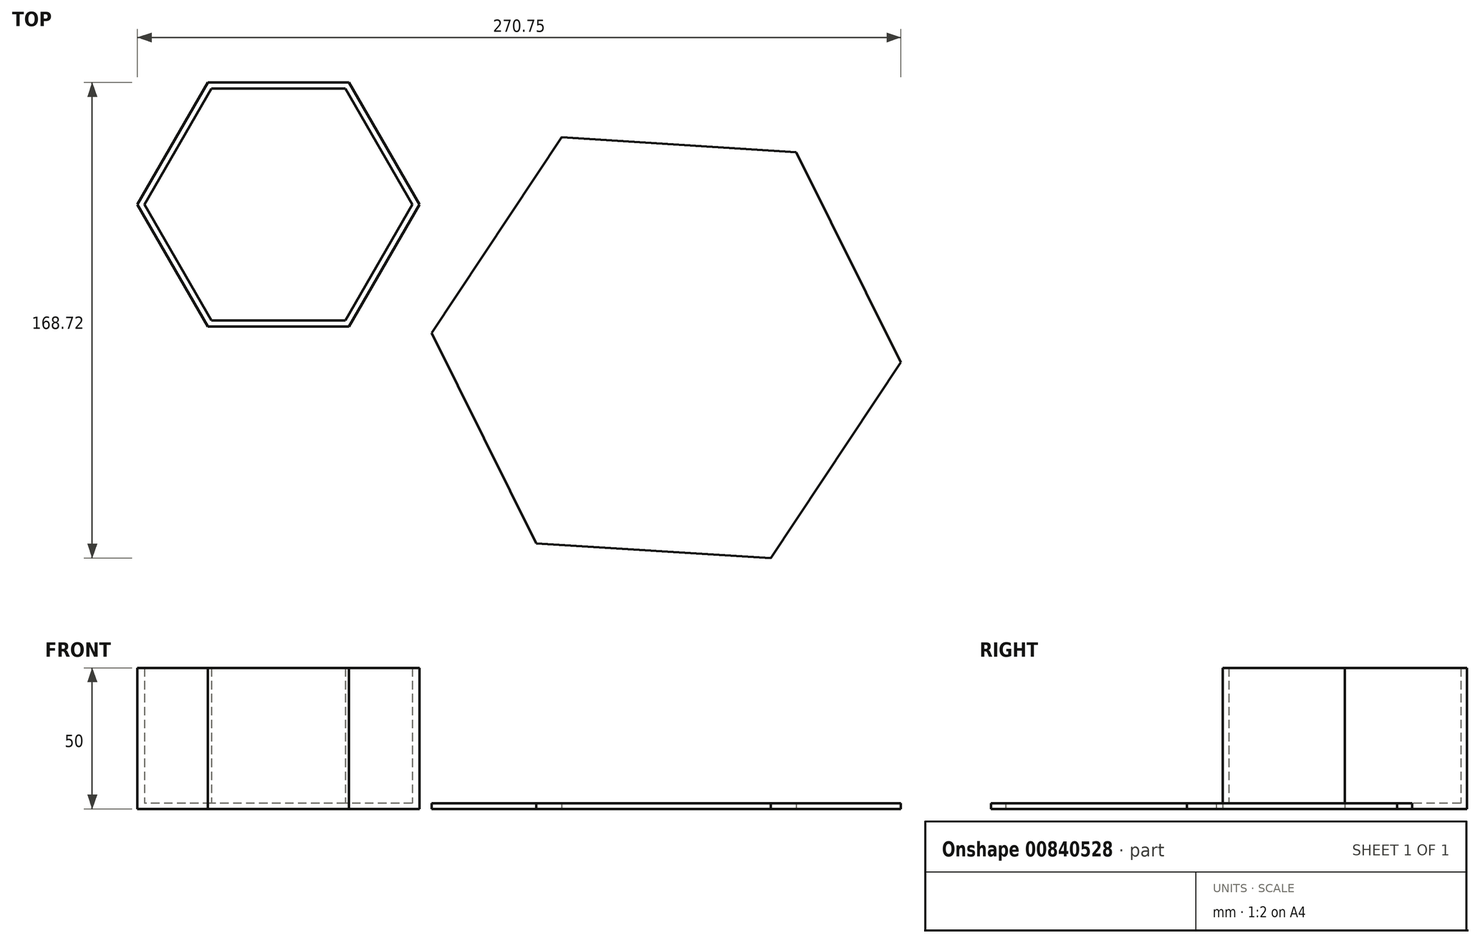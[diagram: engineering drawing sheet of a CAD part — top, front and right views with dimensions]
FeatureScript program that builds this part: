
annotation { "Feature Type Name" : "Feature", "Feature Type Description" : "" }
export const myFeature = defineFeature(function(context is Context, id is Id, definition is map)
    precondition{}
    {
        {
            var Q0;
            Q0=qCreatedBy(makeId("Top.planeOp"),FACE);
            var sketch = newSketch(context, id + "F0", { "sketchPlane" : qUnion([Q0])});
            skCircle(sketch, "E0.cCircle", {"center": v(0, 0) * mm, "radius": 43.3 * mm, "construction": true});
            skLineSegment(sketch, "E0.0", {"start": v(50, 0) * mm, "end": v(25, -43.3) * mm});
            skLineSegment(sketch, "E0.1", {"start": v(25, -43.3) * mm, "end": v(-25, -43.3) * mm});
            skLineSegment(sketch, "E0.2", {"start": v(-25, -43.3) * mm, "end": v(-50, 0) * mm});
            skLineSegment(sketch, "E0.3", {"start": v(-50, 0) * mm, "end": v(-25, 43.3) * mm});
            skLineSegment(sketch, "E0.4", {"start": v(-25, 43.3) * mm, "end": v(25, 43.3) * mm});
            skLineSegment(sketch, "E0.5", {"start": v(25, 43.3) * mm, "end": v(50, 0) * mm});
            skPoint(sketch, "E0.0.midPoint", {"position": v(37.5, -21.65) * mm});
            skCircle(sketch, "E1.cCircle", {"center": v(0, 0) * mm, "radius": 41.14 * mm, "construction": true});
            skLineSegment(sketch, "E1.0", {"start": v(-23.75, 41.14) * mm, "end": v(23.75, 41.14) * mm});
            skLineSegment(sketch, "E1.1", {"start": v(23.75, 41.14) * mm, "end": v(47.5, 0) * mm});
            skLineSegment(sketch, "E1.2", {"start": v(47.5, 0) * mm, "end": v(23.75, -41.14) * mm});
            skLineSegment(sketch, "E1.3", {"start": v(23.75, -41.14) * mm, "end": v(-23.75, -41.14) * mm});
            skLineSegment(sketch, "E1.4", {"start": v(-23.75, -41.14) * mm, "end": v(-47.5, 0) * mm});
            skLineSegment(sketch, "E1.5", {"start": v(-47.5, 0) * mm, "end": v(-23.75, 41.14) * mm});
            skPoint(sketch, "E1.0.midPoint", {"position": v(0, 41.14) * mm});
            skSolve(sketch);
        }
        {
            var Q0;
            Q0 = qSketchRegion(id + "F0", true);
            var Q1;
            Q1=makeQuery(id+"F0.imprint","IMPRINT",FACE,{"disambiguationData":[TD([[makeQuery(id+"F0.imprint","IMPRINT",EDGE,{"derivedFrom":sQuery(id+"F0.wireOp",EDGE,"E1.0")}),-1.0]])]});
            extrude(context, id + "F1", {"entities" : qUnion([Q0, Q1]), "depth" : 2 * mm, "offsetDistance" : 25 * mm});
        }
        {
            var Q0;
            Q0=makeQuery(id+"F0.imprint","IMPRINT",FACE,{"disambiguationData":[TD([[makeQuery(id+"F0.imprint","IMPRINT",EDGE,{"derivedFrom":sQuery(id+"F0.wireOp",EDGE,"E0.0")}),-1.0]])]});
            extrude(context, id + "F2", {"entities" : qUnion([Q0]), "operationType" : NewBodyOperationType.ADD, "depth" : 50 * mm, "offsetDistance" : 25 * mm});
        }
        {
            var Q0;
            Q0=qCreatedBy(makeId("Top.planeOp"),FACE);
            var sketch = newSketch(context, id + "F3", { "sketchPlane" : qUnion([Q0])});
            skCircle(sketch, "E2.cCircle", {"center": v(137.58, -50.78) * mm, "radius": 72.17 * mm, "construction": true});
            skLineSegment(sketch, "E2.0", {"start": v(220.75, -56) * mm, "end": v(174.64, -125.42) * mm});
            skLineSegment(sketch, "E2.1", {"start": v(174.64, -125.42) * mm, "end": v(91.47, -120.2) * mm});
            skLineSegment(sketch, "E2.2", {"start": v(91.47, -120.2) * mm, "end": v(54.4, -45.56) * mm});
            skLineSegment(sketch, "E2.3", {"start": v(54.4, -45.56) * mm, "end": v(100.5, 23.86) * mm});
            skLineSegment(sketch, "E2.4", {"start": v(100.5, 23.86) * mm, "end": v(183.68, 18.64) * mm});
            skLineSegment(sketch, "E2.5", {"start": v(183.68, 18.64) * mm, "end": v(220.75, -56) * mm});
            skPoint(sketch, "E2.0.midPoint", {"position": v(197.7, -90.7) * mm});
            skSolve(sketch);
        }
        {
            var Q0;
            Q0=makeQuery(id+"F3.imprint","IMPRINT",FACE,{"disambiguationData":[TD([[makeQuery(id+"F3.imprint","IMPRINT",EDGE,{"derivedFrom":sQuery(id+"F3.wireOp",EDGE,"E2.0")}),-1.0]])]});
            extrude(context, id + "F4", {"entities" : qUnion([Q0]), "depth" : 2 * mm, "offsetDistance" : 25 * mm});
        }
    });
